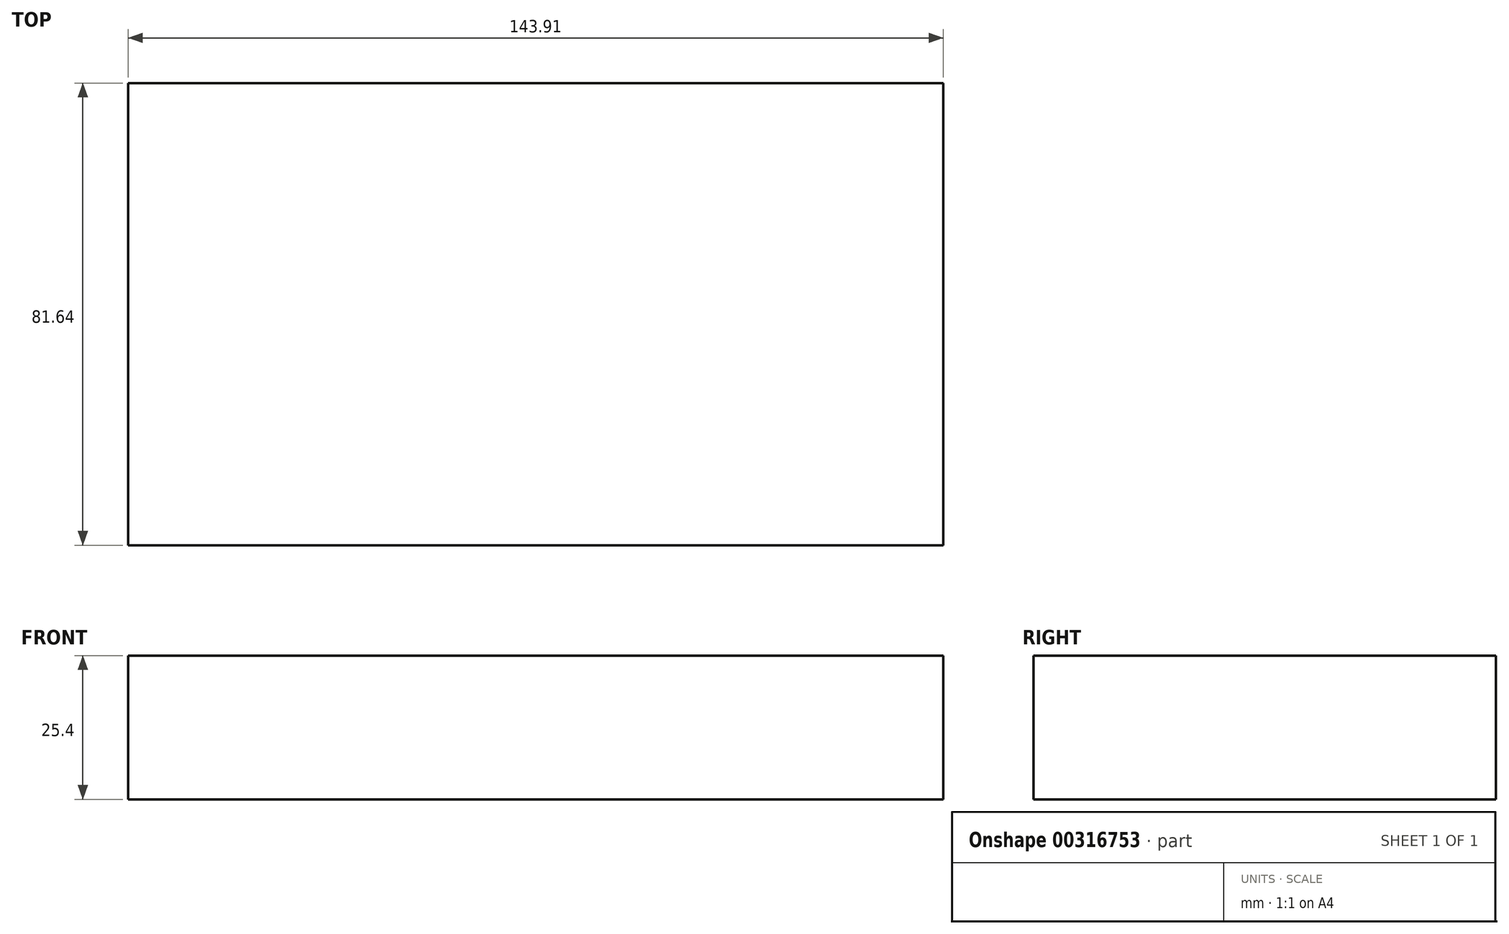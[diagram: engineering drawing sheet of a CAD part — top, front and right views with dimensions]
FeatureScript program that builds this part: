
annotation { "Feature Type Name" : "Feature", "Feature Type Description" : "" }
export const myFeature = defineFeature(function(context is Context, id is Id, definition is map)
    precondition{}
    {
        {
            var Q0;
            Q0=qCreatedBy(makeId("Top.planeOp"),FACE);
            var sketch = newSketch(context, id + "F0", { "sketchPlane" : qUnion([Q0])});
            skLineSegment(sketch, "E0.bottom", {"start": v(-115.26, 30.23) * mm, "end": v(28.65, 30.23) * mm});
            skLineSegment(sketch, "E0.top", {"start": v(-115.26, -51.41) * mm, "end": v(28.65, -51.41) * mm});
            skLineSegment(sketch, "E0.left", {"start": v(-115.26, 30.23) * mm, "end": v(-115.26, -51.41) * mm});
            skLineSegment(sketch, "E0.right", {"start": v(28.65, 30.23) * mm, "end": v(28.65, -51.41) * mm});
            skSolve(sketch);
        }
        {
            var Q0;
            Q0 = qSketchRegion(id + "F0", true);
            extrude(context, id + "F1", {"entities" : qUnion([Q0]), "depth" : 25.4 * mm});
        }
    });
